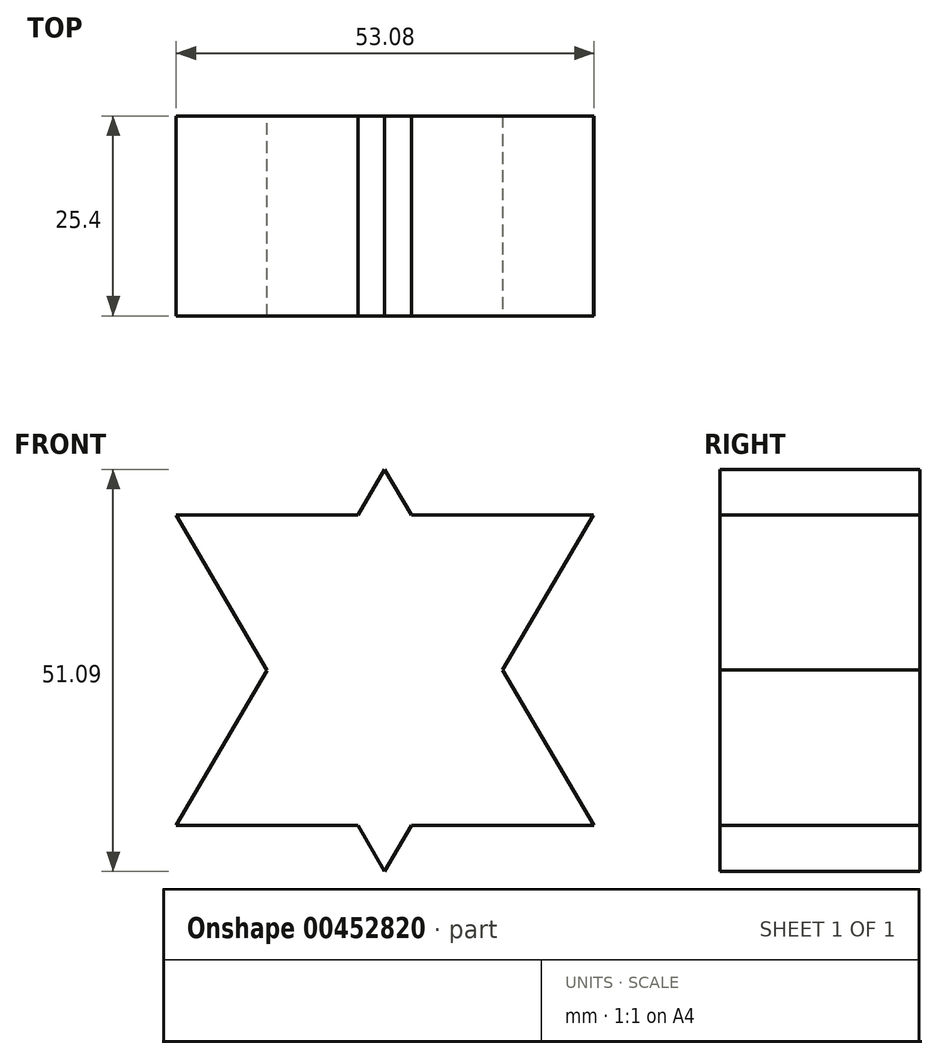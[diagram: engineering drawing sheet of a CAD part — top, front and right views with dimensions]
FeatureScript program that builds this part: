
annotation { "Feature Type Name" : "Feature", "Feature Type Description" : "" }
export const myFeature = defineFeature(function(context is Context, id is Id, definition is map)
    precondition{}
    {
        {
            var Q0;
            Q0=qCreatedBy(makeId("Front.planeOp"),FACE);
            var sketch = newSketch(context, id + "F0", { "sketchPlane" : qUnion([Q0])});
            skLineSegment(sketch, "E0", {"start": v(0, 0) * mm, "end": v(-26.49, 45.3) * mm});
            skLineSegment(sketch, "E1", {"start": v(-26.49, 45.3) * mm, "end": v(26.49, 45.3) * mm});
            skLineSegment(sketch, "E2", {"start": v(0, 0) * mm, "end": v(26.49, 45.3) * mm});
            skLineSegment(sketch, "E3", {"start": v(-26.49, 5.7) * mm, "end": v(26.49, 5.7) * mm, "construction": true});
            skLineSegment(sketch, "E4", {"start": v(-26.49, 5.7) * mm, "end": v(0, 51) * mm, "construction": true});
            skLineSegment(sketch, "E5", {"start": v(26.49, 5.7) * mm, "end": v(0, 51) * mm, "construction": true});
            skSolve(sketch);
        }
        {
            var Q0;
            Q0 = qSketchRegion(id + "F0", true);
            extrude(context, id + "F1", {"entities" : qUnion([Q0]), "depth" : 25.4 * mm});
        }
        {
            var Q0;
            Q0=makeQuery(id+"F1.opExtrude","CAP_FACE",FACE,{"disambiguationData":[OSD([sQuery(id+"F0.wireOp",EDGE,"E0"),sQuery(id+"F0.wireOp",EDGE,"E1"),sQuery(id+"F0.wireOp",EDGE,"E2")])],"isStart":true});
            var sketch = newSketch(context, id + "F2", { "sketchPlane" : qUnion([Q0])});
            skLineSegment(sketch, "E6", {"start": v(26.5, 5.84) * mm, "end": v(0, 51.09) * mm});
            skLineSegment(sketch, "E7", {"start": v(26.5, 5.84) * mm, "end": v(-26.59, 5.84) * mm});
            skLineSegment(sketch, "E8", {"start": v(-26.59, 5.84) * mm, "end": v(0, 51.09) * mm});
            skSolve(sketch);
        }
        {
            var Q0;
            Q0 = qSketchRegion(id + "F2", true);
            extrude(context, id + "F3", {"entities" : qUnion([Q0]), "operationType" : NewBodyOperationType.ADD, "oppositeDirection" : true, "depth" : 25.4 * mm});
        }
    });
